# Revit family: РОСМА_МанометрКоррозионностойкийВиброустойчивый_ЗащитПерегрузк
name_source: partatom
category: Арматура трубопроводов
revit_build: Autodesk Revit 2018 (Build: 20180423_1000(x64)
units: mm (PartAtom-declared; Revit-internal decimal feet)

## family parameters
Всегда вертикально = Да
На основе рабочей плоскости = Нет
Общий = Нет
При загрузке вырезать с полостями = Нет
Размер круглого соединителя = Использовать диаметр
Тип детали = Вставляется

## types (2) — shared parameters
ADSK_Единица измерения = шт.
ADSK_Количество = 1
DN = 15.00 мм
Ddempfer = 6 мм
Table = спец_коррозионностойкий виброустойчивый, с защитой от перегрузки
Table_2 = размеры_коррозионностойкий виброустойчивый, с защитой от перегрузки
URL = https://rosma.spb.ru
Группа модели = Оборудование
Давление02 = ‎ : ТМ 0…0,06МПа
Давление03 = ‎ : ТМ 0…0,1МПа
Давление04 = ‎ : ТМ 0…0,16МПа
Давление05 = ‎ : ТМ 0…0,25МПа
Давление06 = ‎ : ТМ 0…0,4МПа
Давление07 = ‎ : ТМ 0…0,6МПа
Давление08 = ‎ : ТМ 0…1,0МПа
Давление09 = ‎ : ТМ 0…1,6МПа
Давление10 = ‎ : ТМ 0…2,5МПа
Давление11 = ‎ : ТМ 0…4МПа
Давление20 = ‎ : ТМВ -0,1…0,3МПа
Давление21 = ‎ : ТМВ -0,1…0,5МПа
Давление22 = ‎ : ТМВ -0,1…0,9МПа
Давление23 = ‎ : ТМВ -0,1…1,5МПа
Давление24 = ‎ : ТМВ -0,1…2,4МПа
Изготовитель = ЗАО "РОСМА"
Класс точности = 1,0
Климатическое исполнение = Группа Д2 по ГОСТ Р 52931; климатическое исполнение УХЛ категории 1.1 по ГОСТ 15150
Код IP = IP65
Межповерочный интервал = 2 года
Описание = Тип ТМ, серия 21, Пх2,5. Промышленные манометры, устойчивые к воздействию агрессивных измеряемых сред, с возможностью гидрозаполнения (виброустойчивый), для использования в местах с повышенной вибрацией и пульсацией, в случаях, когда возможны кратковременные перегрузки не превышающие 250% от верхнего предела измерений.
Радиальное присоединение = Да
Техническая документация = ТУ 4212-001-4719015564-2008; ГОСТ 2405–88
лого_задн_стенка = Да

## per-type parameters (varying)
| type | Объем заполняемой жидкости |
| 621 | 1000 мл |
| 521 | 360 мл |

note: column(s) folded — value = type name in every type: Исполнение
